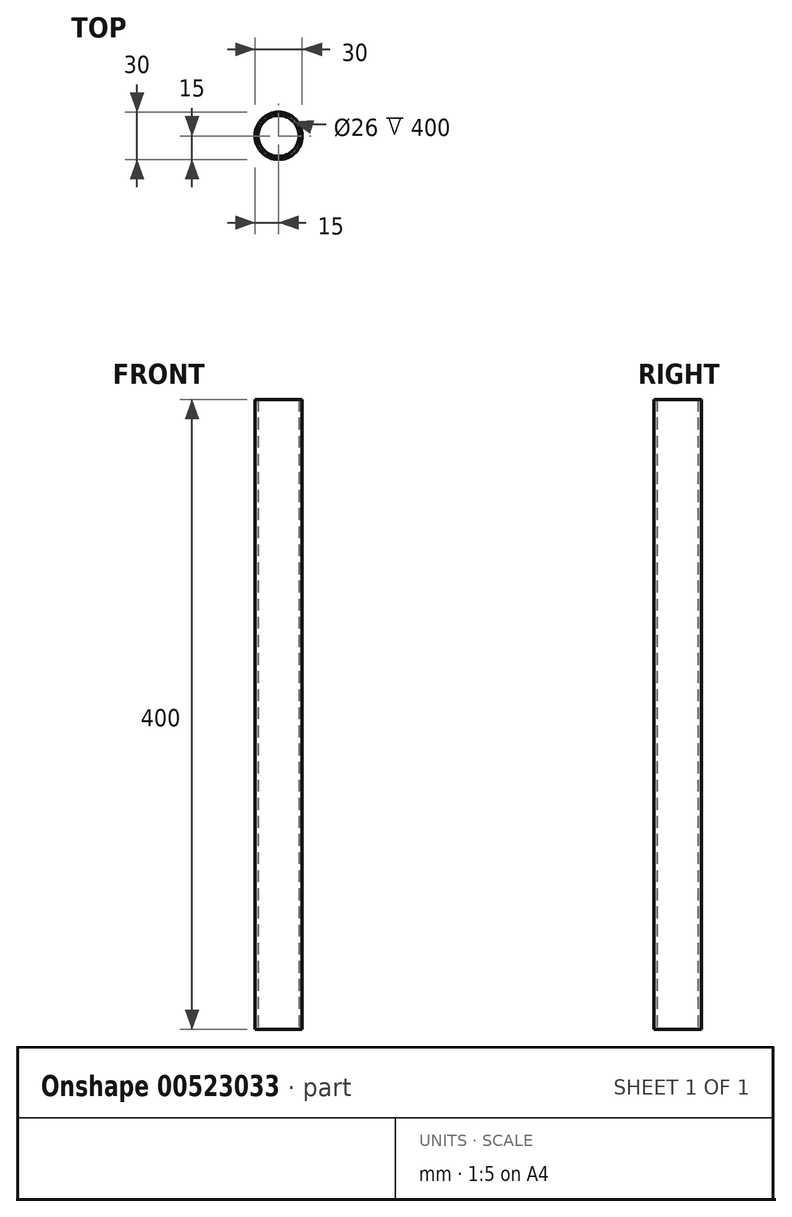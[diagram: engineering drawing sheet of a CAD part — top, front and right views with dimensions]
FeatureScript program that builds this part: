
annotation { "Feature Type Name" : "Feature", "Feature Type Description" : "" }
export const myFeature = defineFeature(function(context is Context, id is Id, definition is map)
    precondition{}
    {
        {
            var Q0;
            Q0=qCreatedBy(makeId("Top.planeOp"),FACE);
            var sketch = newSketch(context, id + "F0", { "sketchPlane" : qUnion([Q0])});
            skCircle(sketch, "E0", {"center": v(0, 0) * mm, "radius": 15 * mm});
            skCircle(sketch, "E1", {"center": v(0, 0) * mm, "radius": 13 * mm});
            skSolve(sketch);
        }
        {
            var Q0;
            Q0=makeQuery(id+"F0.imprint","IMPRINT",FACE,{"disambiguationData":[TD([[makeQuery(id+"F0.imprint","IMPRINT",EDGE,{"derivedFrom":sQuery(id+"F0.wireOp",EDGE,"E0")}),1.0]])]});
            extrude(context, id + "F1", {"entities" : qUnion([Q0]), "depth" : 400 * mm, "offsetDistance" : 25 * mm});
        }
    });
